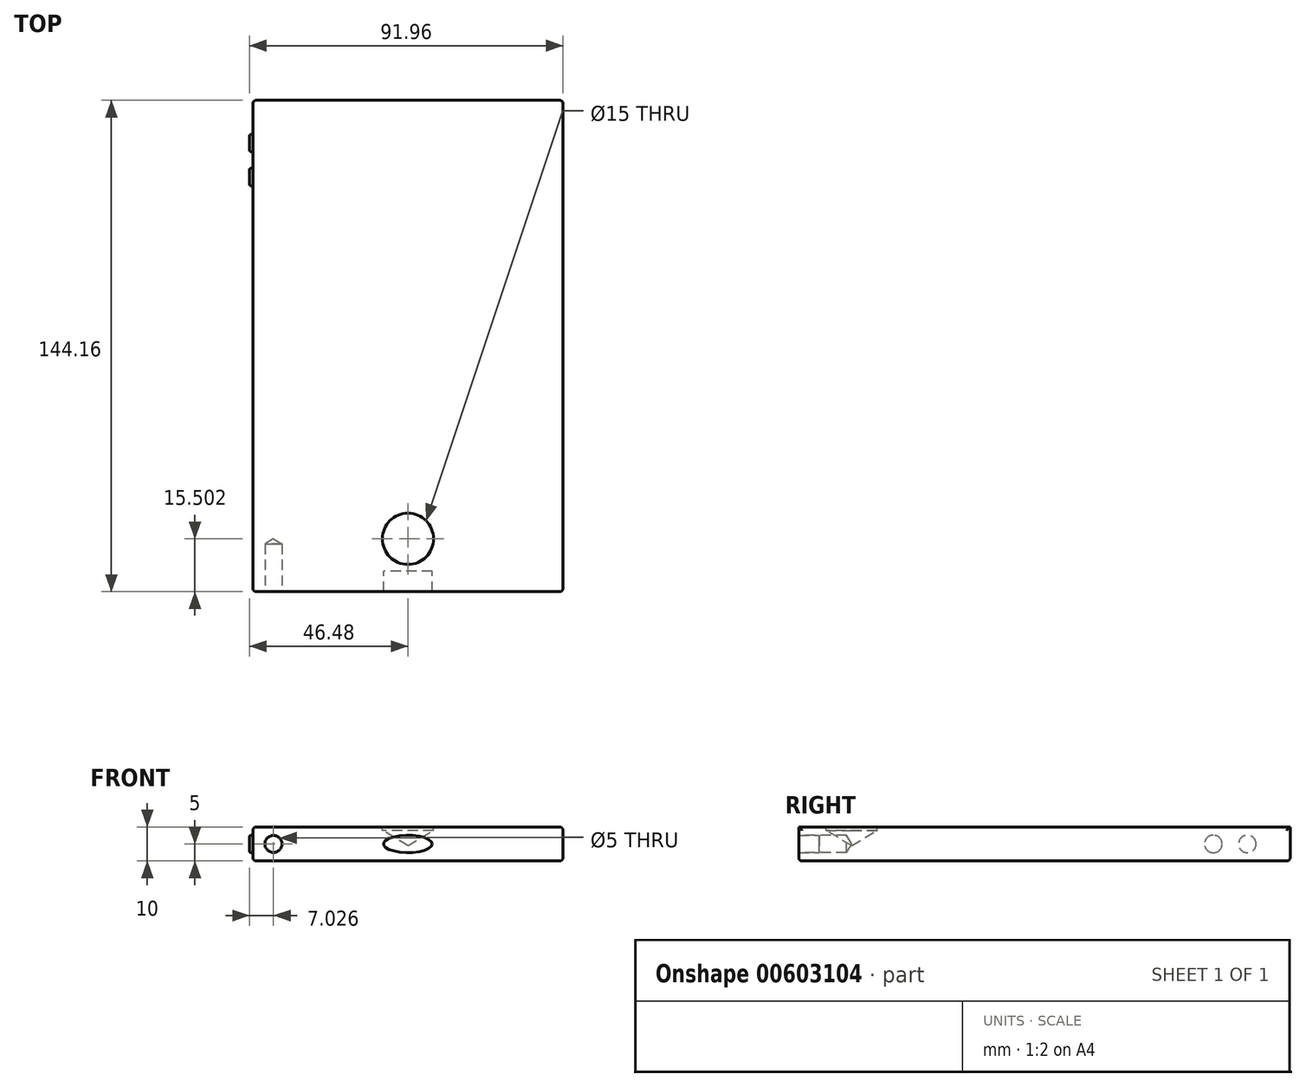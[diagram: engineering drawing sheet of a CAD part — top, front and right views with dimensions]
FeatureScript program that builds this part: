
annotation { "Feature Type Name" : "Feature", "Feature Type Description" : "" }
export const myFeature = defineFeature(function(context is Context, id is Id, definition is map)
    precondition{}
    {
        {
            var Q0;
            Q0=qCreatedBy(makeId("Top.planeOp"),FACE);
            var sketch = newSketch(context, id + "F0", { "sketchPlane" : qUnion([Q0])});
            skLineSegment(sketch, "E0.bottom", {"start": v(-45.48, 69.08) * mm, "end": v(45.48, 69.08) * mm});
            skLineSegment(sketch, "E0.top", {"start": v(-45.48, -69.08) * mm, "end": v(45.48, -69.08) * mm});
            skLineSegment(sketch, "E0.left", {"start": v(-45.48, 69.08) * mm, "end": v(-45.48, -69.08) * mm});
            skLineSegment(sketch, "E0.right", {"start": v(45.48, 69.08) * mm, "end": v(45.48, -69.08) * mm});
            skPoint(sketch, "E0.middle", {"position": v(0, 0) * mm});
            skSolve(sketch);
        }
        {
            var Q0;
            Q0=makeQuery(id+"F0.imprint","IMPRINT",FACE,{"disambiguationData":[TD([[makeQuery(id+"F0.imprint","IMPRINT",EDGE,{"derivedFrom":sQuery(id+"F0.wireOp",EDGE,"E0.bottom")}),-1.0]])]});
            extrude(context, id + "F1", {"entities" : qUnion([Q0]), "depth" : 10 * mm, "offsetDistance" : 25 * mm, "symmetric" : true});
        }
        {
            var Q0;
            Q0=makeQuery(id+"F1.opExtrude","CAP_FACE",FACE,{"disambiguationData":[OSD([sQuery(id+"F0.wireOp",EDGE,"E0.bottom"),sQuery(id+"F0.wireOp",EDGE,"E0.top"),sQuery(id+"F0.wireOp",EDGE,"E0.left"),sQuery(id+"F0.wireOp",EDGE,"E0.right")])],"isStart":false});
            var sketch = newSketch(context, id + "F2", { "sketchPlane" : qUnion([Q0])});
            skCircle(sketch, "E1", {"center": v(0, -59.58) * mm, "radius": 7.57 * mm});
            skSolve(sketch);
        }
        {
            var Q0;
            Q0=makeQuery(id+"F1.opExtrude","SWEPT_FACE",FACE,{"disambiguationData":[OSD([sQuery(id+"F0.wireOp",EDGE,"E0.top")])]});
            var sketch = newSketch(context, id + "F3", { "sketchPlane" : qUnion([Q0])});
            skCircle(sketch, "E2", {"center": v(-39.45, 0) * mm, "radius": 3.3 * mm});
            skSolve(sketch);
        }
        {
            var Q0;
            Q0=sQuery(id+"F3.wireOp",VERTEX,"E2.center");
            var Q1;
            Q1=makeQuery(id+"F1.opExtrude","SWEPT_BODY",BODY,{"disambiguationData":[OSD([sQuery(id+"F0.wireOp",EDGE,"E0.bottom"),sQuery(id+"F0.wireOp",EDGE,"E0.top"),sQuery(id+"F0.wireOp",EDGE,"E0.left"),sQuery(id+"F0.wireOp",EDGE,"E0.right")])]});
            hole(context, id + "F4", {"style" : HoleStyle.SIMPLE, "endStyle" : HoleEndStyle.BLIND, "holeDiameter" : 5 * mm, "majorDiameter" : 5 * mm, "holeDepth" : 8 * mm, "isTappedThrough" : true, "tappedDepth" : 12 * mm, "tapClearance" : 3, "locations" : qUnion([Q0]), "scope" : qUnion([Q1])});
        }
        {
            var Q0;
            Q0=sQuery(id+"F2.wireOp",VERTEX,"E1.center");
            var Q1;
            Q1=makeQuery(id+"F1.opExtrude","SWEPT_BODY",BODY,{"disambiguationData":[OSD([sQuery(id+"F0.wireOp",EDGE,"E0.bottom"),sQuery(id+"F0.wireOp",EDGE,"E0.top"),sQuery(id+"F0.wireOp",EDGE,"E0.left"),sQuery(id+"F0.wireOp",EDGE,"E0.right")])]});
            hole(context, id + "F5", {"style" : HoleStyle.SIMPLE, "endStyle" : HoleEndStyle.BLIND, "holeDiameter" : 15 * mm, "majorDiameter" : 5 * mm, "holeDepth" : 1 * mm, "isTappedThrough" : true, "tappedDepth" : 12 * mm, "tapClearance" : 3, "locations" : qUnion([Q0]), "scope" : qUnion([Q1])});
        }
        {
            var Q0;
            Q0=makeQuery(id+"F1.opExtrude","SWEPT_FACE",FACE,{"disambiguationData":[OSD([sQuery(id+"F0.wireOp",EDGE,"E0.top")])]});
            var sketch = newSketch(context, id + "F6", { "sketchPlane" : qUnion([Q0])});
            skEllipse(sketch, "E3", {"center": v(0, 0) * mm, "majorRadius": 7.13 * mm, "minorRadius": 2.54 * mm, "majorAxis": v(1, 0)});
            skSolve(sketch);
        }
        {
            var Q0;
            Q0=makeQuery(id+"F6.imprint","IMPRINT",FACE,{"disambiguationData":[TD([[makeQuery(id+"F6.imprint","IMPRINT",EDGE,{"derivedFrom":sQuery(id+"F6.wireOp",EDGE,"E3")}),-1.0]])]});
            extrude(context, id + "F7", {"entities" : qUnion([Q0]), "operationType" : NewBodyOperationType.ADD, "depth" : 6 * mm, "offsetDistance" : 25 * mm});
        }
        {
            var Q0;
            {var subQ0=sQuery(id+"F0.wireOp",EDGE,"E0.top");Q0=makeQuery(id+"F7.boolean.opBoolean","MERGE",FACE,{"derivedFrom":[makeQuery(id+"F1.opExtrude","CAP_FACE",FACE,{"disambiguationData":[OSD([sQuery(id+"F0.wireOp",EDGE,"E0.bottom"),subQ0,sQuery(id+"F0.wireOp",EDGE,"E0.left"),sQuery(id+"F0.wireOp",EDGE,"E0.right")])],"isStart":true}),makeQuery(id+"F7.opExtrude","SWEPT_FACE",FACE,{"disambiguationData":[OSD([subQ0]),TDD([makeQuery(id+"F6.imprint","IMPRINT",EDGE,{"derivedFrom":makeQuery(id+"F1.opExtrude","CAP_EDGE",EDGE,{"disambiguationData":[OSD([subQ0])],"isStart":true})})])]})]});}
            fillet(context, id + "F8", {"entities" : qUnion([Q0]), "radius" : 1 * mm, "tangentPropagation" : true, "allowEdgeOverflow" : false});
        }
        {
            var Q0;
            {var subQ0=sQuery(id+"F0.wireOp",EDGE,"E0.right");Q0=makeQuery(id+"F7.boolean.opBoolean","MERGE",FACE,{"derivedFrom":[makeQuery(id+"F1.opExtrude","SWEPT_FACE",FACE,{"disambiguationData":[OSD([subQ0])]}),makeQuery(id+"F7.opExtrude","SWEPT_FACE",FACE,{"disambiguationData":[OSD([sQuery(id+"F0.wireOp",EDGE,"E0.top"),subQ0])]})]});}
            fillet(context, id + "F9", {"entities" : qUnion([Q0]), "radius" : 1 * mm, "tangentPropagation" : true, "allowEdgeOverflow" : false});
        }
        {
            var Q0;
            {var subQ0=sQuery(id+"F0.wireOp",EDGE,"E0.left");Q0=makeQuery(id+"F7.boolean.opBoolean","MERGE",FACE,{"derivedFrom":[makeQuery(id+"F1.opExtrude","SWEPT_FACE",FACE,{"disambiguationData":[OSD([subQ0])]}),makeQuery(id+"F7.opExtrude","SWEPT_FACE",FACE,{"disambiguationData":[OSD([sQuery(id+"F0.wireOp",EDGE,"E0.top"),subQ0])]})]});}
            fillet(context, id + "F10", {"entities" : qUnion([Q0]), "radius" : 1 * mm, "tangentPropagation" : true, "allowEdgeOverflow" : false});
        }
        {
            var Q0;
            {var subQ0=sQuery(id+"F0.wireOp",EDGE,"E0.left");Q0=makeQuery(id+"F7.boolean.opBoolean","MERGE",FACE,{"derivedFrom":[makeQuery(id+"F1.opExtrude","SWEPT_FACE",FACE,{"disambiguationData":[OSD([subQ0])]}),makeQuery(id+"F7.opExtrude","SWEPT_FACE",FACE,{"disambiguationData":[OSD([sQuery(id+"F0.wireOp",EDGE,"E0.top"),subQ0])]})]});}
            var sketch = newSketch(context, id + "F11", { "sketchPlane" : qUnion([Q0])});
            skCircle(sketch, "E4", {"center": v(-56.52, 0) * mm, "radius": 2.55 * mm});
            skSolve(sketch);
        }
        {
            var Q0;
            Q0=makeQuery(id+"F11.imprint","IMPRINT",FACE,{"disambiguationData":[TD([[makeQuery(id+"F11.imprint","IMPRINT",EDGE,{"derivedFrom":sQuery(id+"F11.wireOp",EDGE,"E4")}),1.0]])]});
            extrude(context, id + "F12", {"entities" : qUnion([Q0]), "operationType" : NewBodyOperationType.ADD, "depth" : 1 * mm, "offsetDistance" : 25 * mm});
        }
        {
            var Q0;
            {var subQ0=sQuery(id+"F0.wireOp",EDGE,"E0.left");Q0=makeQuery(id+"F7.boolean.opBoolean","MERGE",FACE,{"derivedFrom":[makeQuery(id+"F1.opExtrude","SWEPT_FACE",FACE,{"disambiguationData":[OSD([subQ0])]}),makeQuery(id+"F7.opExtrude","SWEPT_FACE",FACE,{"disambiguationData":[OSD([sQuery(id+"F0.wireOp",EDGE,"E0.top"),subQ0])]})]});}
            var sketch = newSketch(context, id + "F13", { "sketchPlane" : qUnion([Q0])});
            skCircle(sketch, "E5", {"center": v(-46.54, 0) * mm, "radius": 2.58 * mm});
            skSolve(sketch);
        }
        {
            var Q0;
            Q0=makeQuery(id+"F13.imprint","IMPRINT",FACE,{"disambiguationData":[TD([[makeQuery(id+"F13.imprint","IMPRINT",EDGE,{"derivedFrom":sQuery(id+"F13.wireOp",EDGE,"E5")}),1.0]])]});
            extrude(context, id + "F14", {"entities" : qUnion([Q0]), "operationType" : NewBodyOperationType.ADD, "depth" : 1 * mm, "offsetDistance" : 25 * mm});
        }
        {
            var Q0;
            Q0=makeQuery(id+"F12.opExtrude","CAP_EDGE",EDGE,{"disambiguationData":[OSD([sQuery(id+"F11.wireOp",EDGE,"E4")])],"isStart":false});
            fillet(context, id + "F15", {"entities" : qUnion([Q0]), "radius" : 0.5 * mm, "tangentPropagation" : true, "allowEdgeOverflow" : false});
        }
        {
            var Q0;
            Q0=makeQuery(id+"F14.opExtrude","CAP_EDGE",EDGE,{"disambiguationData":[OSD([sQuery(id+"F13.wireOp",EDGE,"E5")])],"isStart":false});
            fillet(context, id + "F16", {"entities" : qUnion([Q0]), "radius" : 0.5 * mm, "tangentPropagation" : true, "allowEdgeOverflow" : false});
        }
    });
